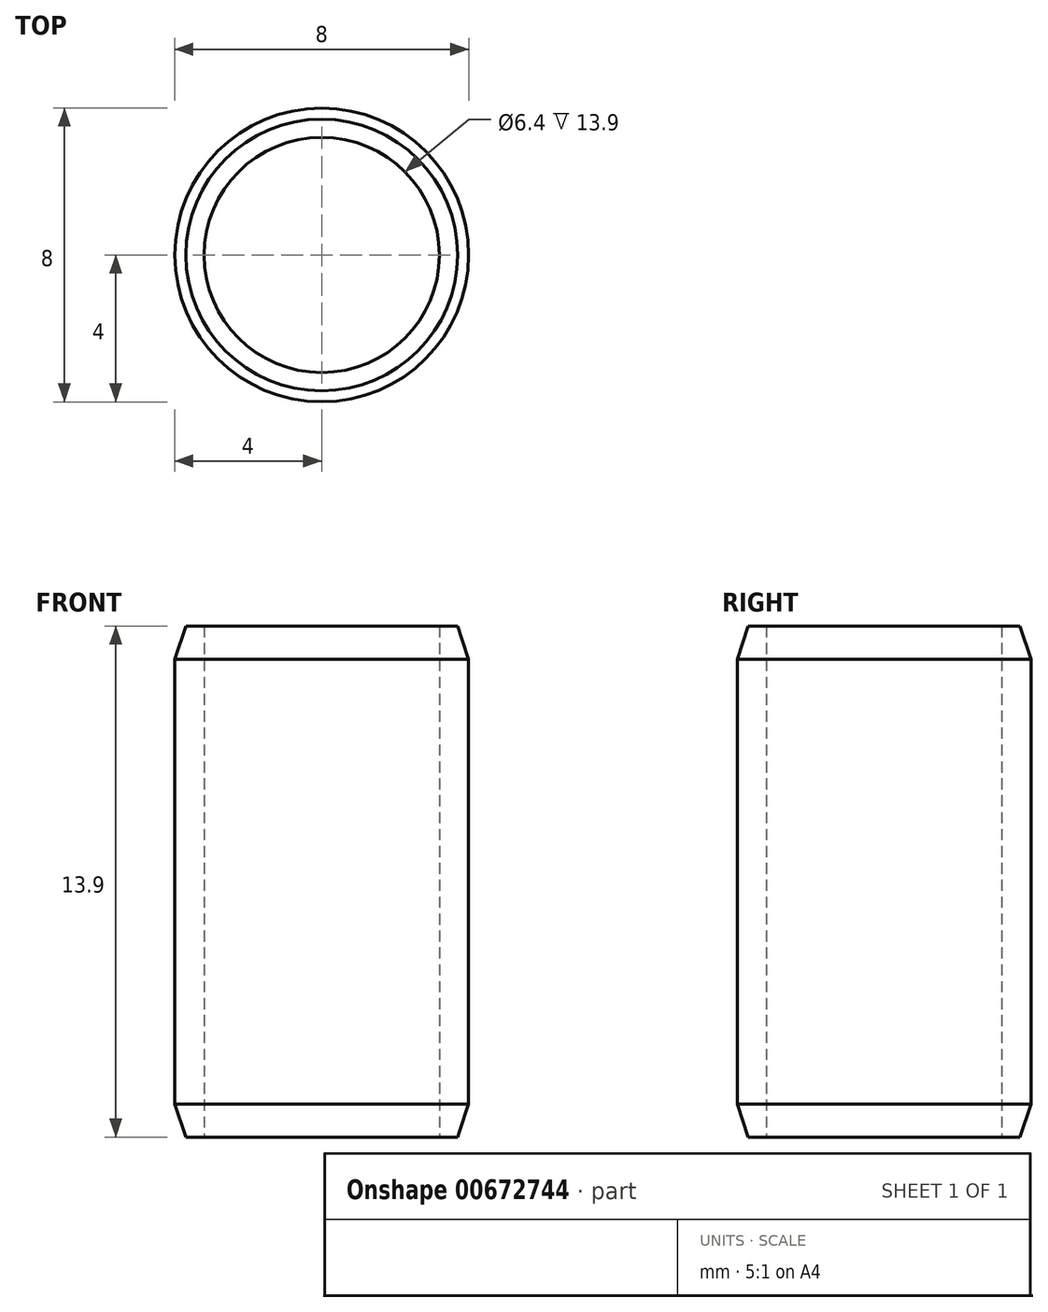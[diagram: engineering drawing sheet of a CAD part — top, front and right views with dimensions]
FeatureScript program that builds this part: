
annotation { "Feature Type Name" : "Feature", "Feature Type Description" : "" }
export const myFeature = defineFeature(function(context is Context, id is Id, definition is map)
    precondition{}
    {
        {
            var Q0;
            Q0=qCreatedBy(makeId("Top.planeOp"),FACE);
            var sketch = newSketch(context, id + "F0", { "sketchPlane" : qUnion([Q0])});
            skCircle(sketch, "E0", {"center": v(0, 0) * mm, "radius": 3.2 * mm});
            skCircle(sketch, "E1", {"center": v(0, 0) * mm, "radius": 4 * mm});
            skSolve(sketch);
        }
        {
            var Q0;
            Q0 = qSketchRegion(id + "F0", true);
            extrude(context, id + "F1", {"entities" : qUnion([Q0]), "depth" : 13.9 * mm, "offsetDistance" : 25 * mm});
        }
        {
            var Q0;
            Q0=makeQuery(id+"F1.opExtrude","CAP_EDGE",EDGE,{"disambiguationData":[OSD([sQuery(id+"F0.wireOp",EDGE,"E1")])],"isStart":false});
            var Q1;
            Q1=makeQuery(id+"F1.opExtrude","CAP_EDGE",EDGE,{"disambiguationData":[OSD([sQuery(id+"F0.wireOp",EDGE,"E1")])],"isStart":true});
            chamfer(context, id + "F2", {"entities" : qUnion([Q0, Q1]), "chamferType" : ChamferType.TWO_OFFSETS, "width1" : 0.3 * mm, "oppositeDirection" : false, "width2" : 0.9 * mm, "tangentPropagation" : true});
        }
    });
